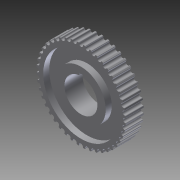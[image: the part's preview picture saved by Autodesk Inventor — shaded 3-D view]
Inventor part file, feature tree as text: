
AUTODESK INVENTOR PART (.ipt)
format: ipt  version: 2012 (Build 160160000, 160)  size: 380,928 bytes
history: native  units: in
note: dims shown in document units (in); Inventor stores cm internally (conversion verified against a paired STEP export)
features: extrude x2, sketch x1, imported_body x1
ambient origin geometry x8: Origin, YZ Plane, XZ Plane, XY Plane, X Axis, Y Axis, Z Axis, Center Point
feature tree (4):
  sketch  "Sketch1"  dims[d0=1.0in d1=0.125in d2=0.0625in d3=0.5625in d4=0.39in d5=0.0in d6=0.39in d7=0.0in]
  extrude  "Extrusion1"  Depth=0.125in
  extrude  "Extrusion2"  Depth=0.0625in
  imported_body  "Base1"
